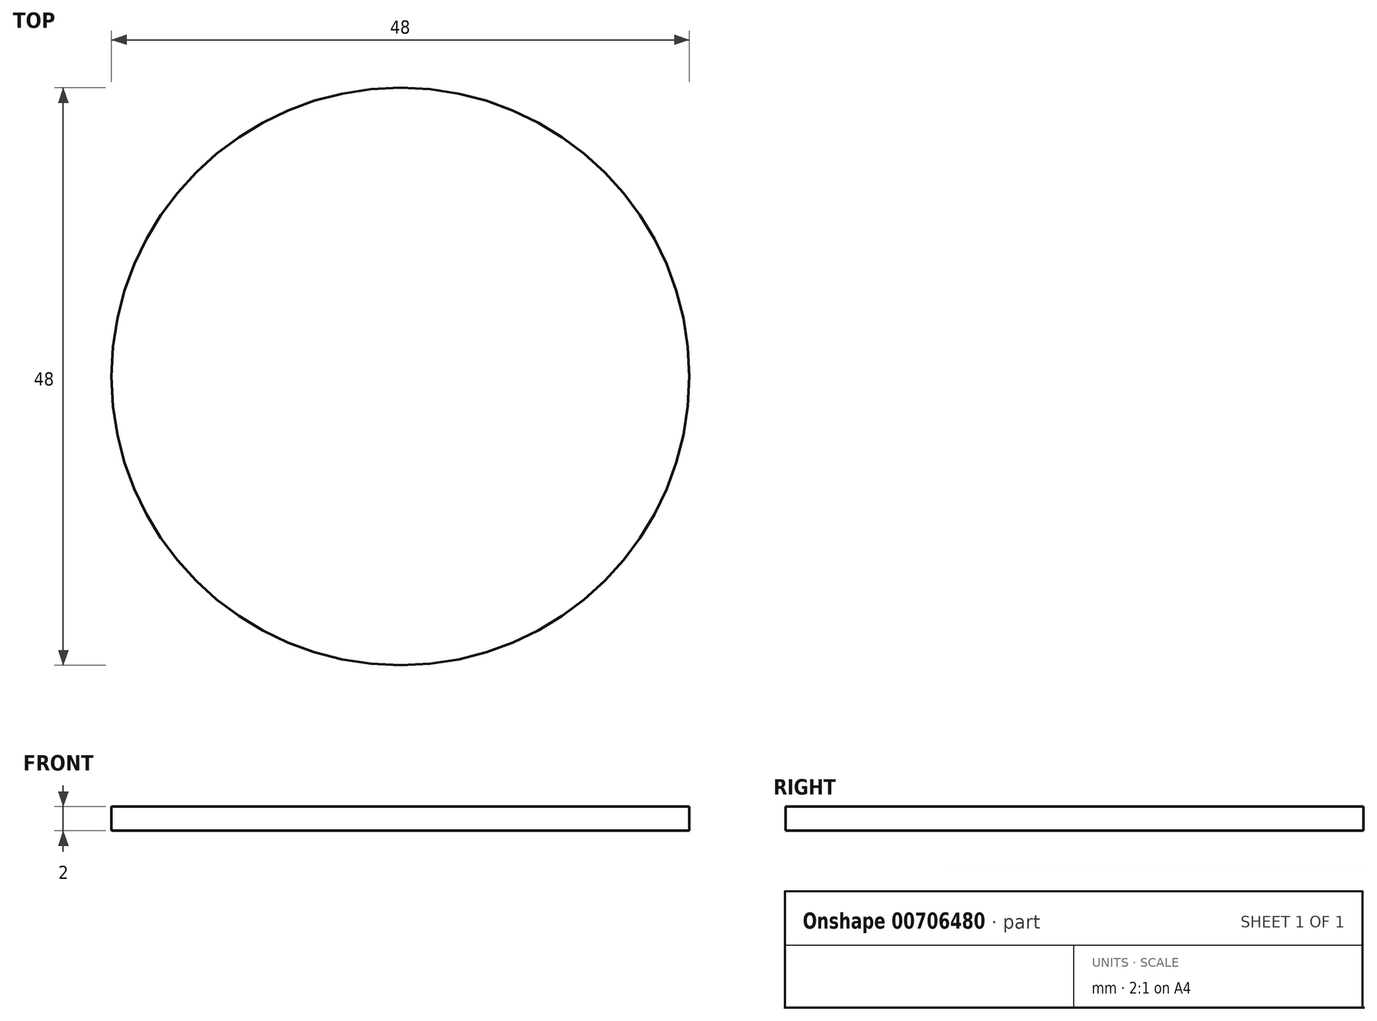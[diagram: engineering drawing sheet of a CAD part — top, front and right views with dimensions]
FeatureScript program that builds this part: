
annotation { "Feature Type Name" : "Feature", "Feature Type Description" : "" }
export const myFeature = defineFeature(function(context is Context, id is Id, definition is map)
    precondition{}
    {
        {
            var Q0;
            Q0=qCreatedBy(makeId("Top.planeOp"),FACE);
            var sketch = newSketch(context, id + "F0", { "sketchPlane" : qUnion([Q0])});
            skCircle(sketch, "E0", {"center": v(0, 0) * mm, "radius": 24 * mm});
            skSolve(sketch);
        }
        {
            var Q0;
            Q0 = qSketchRegion(id + "F0", true);
            extrude(context, id + "F1", {"entities" : qUnion([Q0]), "depth" : 2 * mm, "offsetDistance" : 25 * mm});
        }
    });
